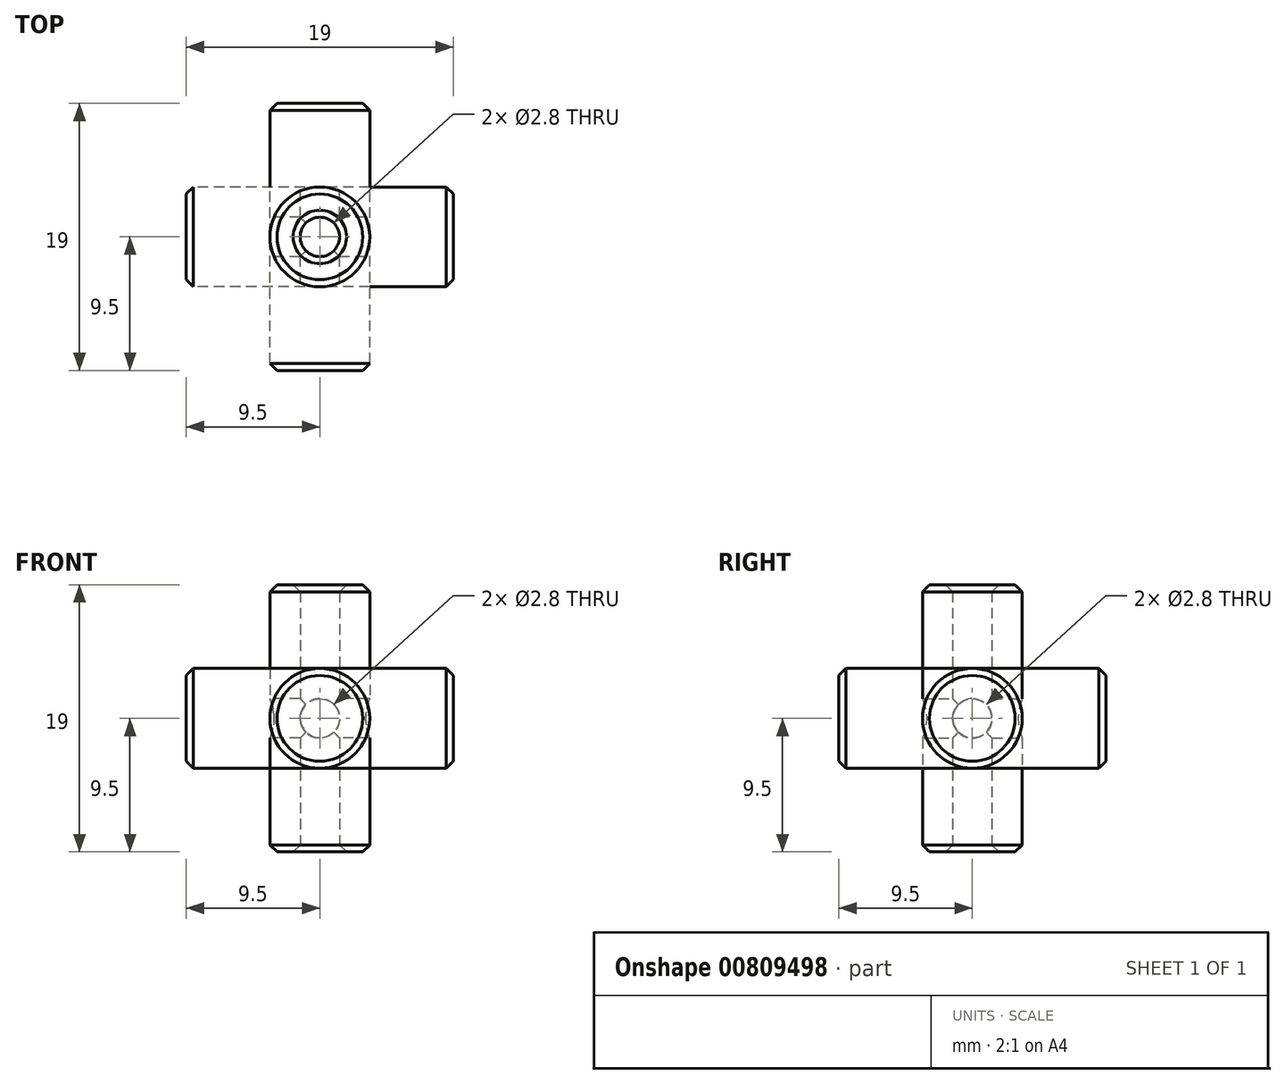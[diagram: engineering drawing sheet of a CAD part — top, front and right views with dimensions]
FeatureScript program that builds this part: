
annotation { "Feature Type Name" : "Feature", "Feature Type Description" : "" }
export const myFeature = defineFeature(function(context is Context, id is Id, definition is map)
    precondition{}
    {
        {
            var Q0;
            Q0=qCreatedBy(makeId("Front.planeOp"),FACE);
            var sketch = newSketch(context, id + "F0", { "sketchPlane" : qUnion([Q0])});
            skCircle(sketch, "E0", {"center": v(0, 0) * mm, "radius": 1.4 * mm});
            skSolve(sketch);
        }
        {
            var Q0;
            Q0=qCreatedBy(makeId("Front.planeOp"),FACE);
            var sketch = newSketch(context, id + "F1", { "sketchPlane" : qUnion([Q0])});
            skCircle(sketch, "E1", {"center": v(0, 0) * mm, "radius": 3.55 * mm});
            skSolve(sketch);
        }
        {
            var Q0;
            Q0=makeQuery(id+"F1.imprint","IMPRINT",FACE,{"disambiguationData":[TD([[makeQuery(id+"F1.imprint","IMPRINT",EDGE,{"derivedFrom":sQuery(id+"F1.wireOp",EDGE,"E1")}),1.0]])]});
            extrude(context, id + "F2", {"entities" : qUnion([Q0]), "endBound" : BoundingType.SYMMETRIC, "depth" : 19 * mm, "offsetDistance" : 25 * mm});
        }
        {
            var Q0;
            Q0 = qSketchRegion(id + "F0", true);
            extrude(context, id + "F3", {"entities" : qUnion([Q0]), "endBound" : BoundingType.SYMMETRIC, "depth" : 20 * mm, "offsetDistance" : 25 * mm});
        }
        {
            var Q0;
            Q0=qCreatedBy(makeId("Front.planeOp"),FACE);
            var sketch = newSketch(context, id + "F4", { "sketchPlane" : qUnion([Q0])});
            skLineSegment(sketch, "E2.bottom", {"start": v(0, 0) * mm, "end": v(10, 0) * mm});
            skLineSegment(sketch, "E2.top", {"start": v(0, 10) * mm, "end": v(10, 10) * mm});
            skLineSegment(sketch, "E2.left", {"start": v(0, 0) * mm, "end": v(0, 10) * mm});
            skLineSegment(sketch, "E2.right", {"start": v(10, 0) * mm, "end": v(10, 10) * mm});
            skSolve(sketch);
        }
        {
            var Q0;
            Q0=makeQuery(id+"F4.imprint","IMPRINT",FACE,{"disambiguationData":[TD([[makeQuery(id+"F4.imprint","IMPRINT",EDGE,{"derivedFrom":sQuery(id+"F4.wireOp",EDGE,"E2.bottom")}),1.0]])]});
            extrude(context, id + "F5", {"entities" : qUnion([Q0]), "depth" : 10 * mm, "offsetDistance" : 25 * mm});
        }
        {
            var Q0;
            Q0=makeQuery(id+"F5.opExtrude","CAP_VERTEX",VERTEX,{"disambiguationData":[OSD([sQuery(id+"F4.wireOp",EDGE,"E2.top"),sQuery(id+"F4.wireOp",EDGE,"E2.right")])],"isStart":false});
            var Q1;
            Q1=qCreatedBy(makeId("Origin.pointOp"),VERTEX);
            var Q2;
            Q2=makeQuery(id+"F5.opExtrude","CAP_VERTEX",VERTEX,{"disambiguationData":[OSD([sQuery(id+"F4.wireOp",EDGE,"E2.bottom"),sQuery(id+"F4.wireOp",EDGE,"E2.right")])],"isStart":false});
            cPlane(context, id + "F6", {"entities" : qUnion([Q0, Q1, Q2]), "cplaneType" : CPlaneType.THREE_POINT, "offset" : 25 * mm, "width" : 150 * mm, "height" : 150 * mm});
        }
        {
            var Q0;
            Q0=qCreatedBy(id+"F6.planeOp",FACE);
            var sketch = newSketch(context, id + "F7", { "sketchPlane" : qUnion([Q0])});
            skLineSegment(sketch, "E3", {"start": v(0, 0) * mm, "end": v(-14.14, 10) * mm});
            skSolve(sketch);
        }
        {
            var Q0;
            Q0=makeQuery(id+"F5.opExtrude","SWEPT_BODY",BODY,{"disambiguationData":[OSD([sQuery(id+"F4.wireOp",EDGE,"E2.bottom"),sQuery(id+"F4.wireOp",EDGE,"E2.top"),sQuery(id+"F4.wireOp",EDGE,"E2.left"),sQuery(id+"F4.wireOp",EDGE,"E2.right")])]});
            deleteBodies(context, id + "F8", {"entities" : qUnion([Q0])});
        }
        {
            var Q0;
            Q0=makeQuery(id+"F2.opExtrude","SWEPT_BODY",BODY,{"disambiguationData":[OSD([sQuery(id+"F1.wireOp",EDGE,"E1")])]});
            var Q1;
            Q1=makeQuery(id+"F3.opExtrude","SWEPT_BODY",BODY,{"disambiguationData":[OSD([sQuery(id+"F0.wireOp",EDGE,"E0")])]});
            var Q2;
            Q2=sQuery(id+"F7.wireOp",EDGE,"E3");
            circularPattern(context, id + "F9", {"entities" : qUnion([Q0, Q1]), "axis" : qUnion([Q2]), "angle" : 360 * degree, "instanceCount" : 3, "equalSpace" : true});
        }
        {
            var Q0;
            Q0=makeQuery(id+"F9.opPattern","COPY",BODY,{"derivedFrom":makeQuery(id+"F3.opExtrude","SWEPT_BODY",BODY,{"disambiguationData":[OSD([sQuery(id+"F0.wireOp",EDGE,"E0")])]}),"instanceName":"2"});
            var Q1;
            Q1=makeQuery(id+"F3.opExtrude","SWEPT_BODY",BODY,{"disambiguationData":[OSD([sQuery(id+"F0.wireOp",EDGE,"E0")])]});
            var Q2;
            Q2=makeQuery(id+"F9.opPattern","COPY",BODY,{"derivedFrom":makeQuery(id+"F3.opExtrude","SWEPT_BODY",BODY,{"disambiguationData":[OSD([sQuery(id+"F0.wireOp",EDGE,"E0")])]}),"instanceName":"1"});
            var Q3;
            Q3=makeQuery(id+"F9.opPattern","COPY",BODY,{"derivedFrom":makeQuery(id+"F2.opExtrude","SWEPT_BODY",BODY,{"disambiguationData":[OSD([sQuery(id+"F1.wireOp",EDGE,"E1")])]}),"instanceName":"2"});
            booleanBodies(context, id + "F10", {"operationType" : BooleanOperationType.SUBTRACTION, "tools" : qUnion([Q0, Q1, Q2]), "targets" : qUnion([Q3])});
        }
        {
            var Q0;
            Q0=makeQuery(id+"F9.opPattern","COPY",FACE,{"derivedFrom":makeQuery(id+"F2.opExtrude","CAP_FACE",FACE,{"disambiguationData":[OSD([sQuery(id+"F1.wireOp",EDGE,"E1")])],"isStart":true}),"instanceName":"1"});
            var Q1;
            Q1=makeQuery(id+"F10.opBoolean","INTERSECT",EDGE,{"derivedFrom":[makeQuery(id+"F9.opPattern","COPY",FACE,{"derivedFrom":makeQuery(id+"F2.opExtrude","CAP_FACE",FACE,{"disambiguationData":[OSD([sQuery(id+"F1.wireOp",EDGE,"E1")])],"isStart":true}),"instanceName":"1"}),makeQuery(id+"F9.opPattern","COPY",FACE,{"derivedFrom":makeQuery(id+"F3.opExtrude","SWEPT_FACE",FACE,{"disambiguationData":[OSD([sQuery(id+"F0.wireOp",EDGE,"E0")])]}),"instanceName":"1"})]});
            var Q2;
            Q2=makeQuery(id+"F10.opBoolean","INTERSECT",EDGE,{"derivedFrom":[makeQuery(id+"F2.opExtrude","CAP_FACE",FACE,{"disambiguationData":[OSD([sQuery(id+"F1.wireOp",EDGE,"E1")])],"isStart":false}),makeQuery(id+"F3.opExtrude","SWEPT_FACE",FACE,{"disambiguationData":[OSD([sQuery(id+"F0.wireOp",EDGE,"E0")])]})]});
            var Q3;
            Q3=makeQuery(id+"F2.opExtrude","CAP_EDGE",EDGE,{"disambiguationData":[OSD([sQuery(id+"F1.wireOp",EDGE,"E1")])],"isStart":false});
            var Q4;
            Q4=makeQuery(id+"F9.opPattern","COPY",EDGE,{"derivedFrom":makeQuery(id+"F2.opExtrude","CAP_EDGE",EDGE,{"disambiguationData":[OSD([sQuery(id+"F1.wireOp",EDGE,"E1")])],"isStart":false}),"instanceName":"2"});
            var Q5;
            Q5=makeQuery(id+"F10.opBoolean","INTERSECT",EDGE,{"derivedFrom":[makeQuery(id+"F9.opPattern","COPY",FACE,{"derivedFrom":makeQuery(id+"F2.opExtrude","CAP_FACE",FACE,{"disambiguationData":[OSD([sQuery(id+"F1.wireOp",EDGE,"E1")])],"isStart":false}),"instanceName":"2"}),makeQuery(id+"F9.opPattern","COPY",FACE,{"derivedFrom":makeQuery(id+"F3.opExtrude","SWEPT_FACE",FACE,{"disambiguationData":[OSD([sQuery(id+"F0.wireOp",EDGE,"E0")])]}),"instanceName":"2"})]});
            var Q6;
            Q6=makeQuery(id+"F9.opPattern","COPY",EDGE,{"derivedFrom":makeQuery(id+"F2.opExtrude","CAP_EDGE",EDGE,{"disambiguationData":[OSD([sQuery(id+"F1.wireOp",EDGE,"E1")])],"isStart":false}),"instanceName":"1"});
            var Q7;
            Q7=makeQuery(id+"F10.opBoolean","INTERSECT",EDGE,{"derivedFrom":[makeQuery(id+"F9.opPattern","COPY",FACE,{"derivedFrom":makeQuery(id+"F2.opExtrude","CAP_FACE",FACE,{"disambiguationData":[OSD([sQuery(id+"F1.wireOp",EDGE,"E1")])],"isStart":false}),"instanceName":"1"}),makeQuery(id+"F9.opPattern","COPY",FACE,{"derivedFrom":makeQuery(id+"F3.opExtrude","SWEPT_FACE",FACE,{"disambiguationData":[OSD([sQuery(id+"F0.wireOp",EDGE,"E0")])]}),"instanceName":"1"})]});
            var Q8;
            Q8=makeQuery(id+"F2.opExtrude","CAP_EDGE",EDGE,{"disambiguationData":[OSD([sQuery(id+"F1.wireOp",EDGE,"E1")])],"isStart":true});
            var Q9;
            Q9=makeQuery(id+"F10.opBoolean","INTERSECT",EDGE,{"derivedFrom":[makeQuery(id+"F2.opExtrude","CAP_FACE",FACE,{"disambiguationData":[OSD([sQuery(id+"F1.wireOp",EDGE,"E1")])],"isStart":true}),makeQuery(id+"F3.opExtrude","SWEPT_FACE",FACE,{"disambiguationData":[OSD([sQuery(id+"F0.wireOp",EDGE,"E0")])]})]});
            var Q10;
            Q10=makeQuery(id+"F9.opPattern","COPY",EDGE,{"derivedFrom":makeQuery(id+"F2.opExtrude","CAP_EDGE",EDGE,{"disambiguationData":[OSD([sQuery(id+"F1.wireOp",EDGE,"E1")])],"isStart":true}),"instanceName":"2"});
            var Q11;
            Q11=makeQuery(id+"F10.opBoolean","INTERSECT",EDGE,{"derivedFrom":[makeQuery(id+"F9.opPattern","COPY",FACE,{"derivedFrom":makeQuery(id+"F2.opExtrude","CAP_FACE",FACE,{"disambiguationData":[OSD([sQuery(id+"F1.wireOp",EDGE,"E1")])],"isStart":true}),"instanceName":"2"}),makeQuery(id+"F9.opPattern","COPY",FACE,{"derivedFrom":makeQuery(id+"F3.opExtrude","SWEPT_FACE",FACE,{"disambiguationData":[OSD([sQuery(id+"F0.wireOp",EDGE,"E0")])]}),"instanceName":"2"})]});
            chamfer(context, id + "F11", {"entities" : qUnion([Q0, Q1, Q2, Q3, Q4, Q5, Q6, Q7, Q8, Q9, Q10, Q11]), "width" : 0.5 * mm, "tangentPropagation" : true});
        }
    });
